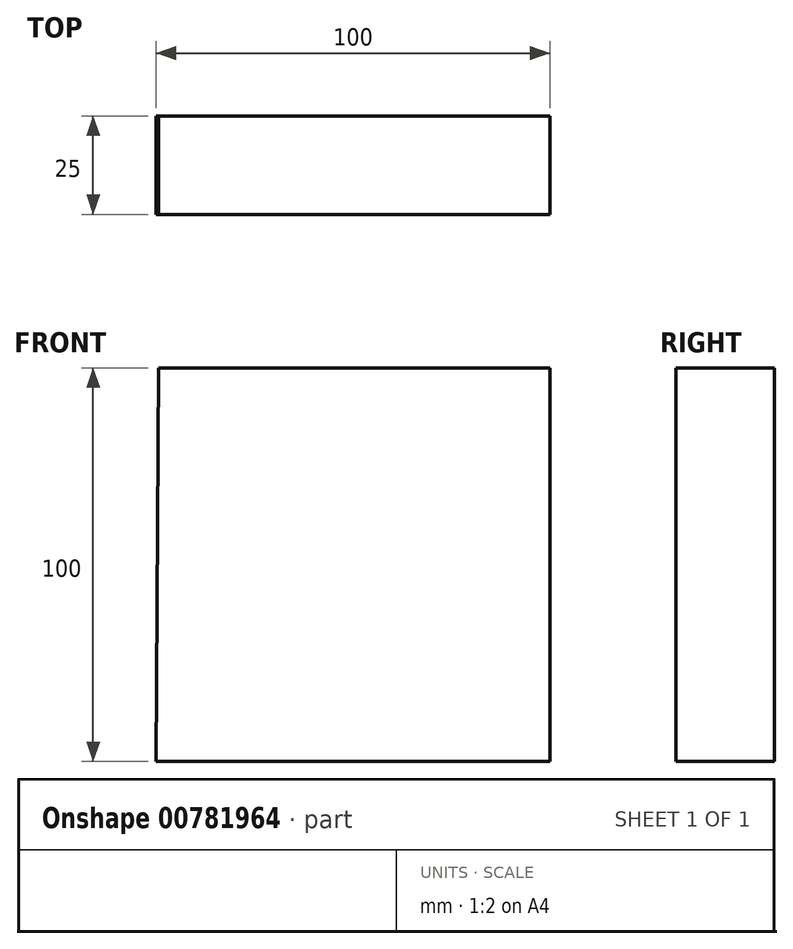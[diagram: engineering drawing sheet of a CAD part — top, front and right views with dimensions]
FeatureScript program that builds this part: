
annotation { "Feature Type Name" : "Feature", "Feature Type Description" : "" }
export const myFeature = defineFeature(function(context is Context, id is Id, definition is map)
    precondition{}
    {
        {
            var Q0;
            Q0=qCreatedBy(makeId("Front.planeOp"),FACE);
            var sketch = newSketch(context, id + "F0", { "sketchPlane" : qUnion([Q0])});
            skLineSegment(sketch, "E0.bottom", {"start": v(11.7, 87.23) * mm, "end": v(-87.64, 87.23) * mm});
            skLineSegment(sketch, "E0.top", {"start": v(11.7, -12.77) * mm, "end": v(-88.3, -12.77) * mm});
            skLineSegment(sketch, "E0.left", {"start": v(11.7, 87.23) * mm, "end": v(11.7, -12.77) * mm});
            skLineSegment(sketch, "E0.right", {"start": v(-87.64, 87.23) * mm, "end": v(-88.3, -12.77) * mm});
            skSolve(sketch);
        }
        {
            var Q0;
            Q0=qSketchRegion(id+"F0",true);
            extrude(context, id + "F1", {"entities" : qUnion([Q0]), "endBound" : BoundingType.SYMMETRIC, "depth" : 25 * mm, "offsetDistance" : 25 * mm});
        }
    });
